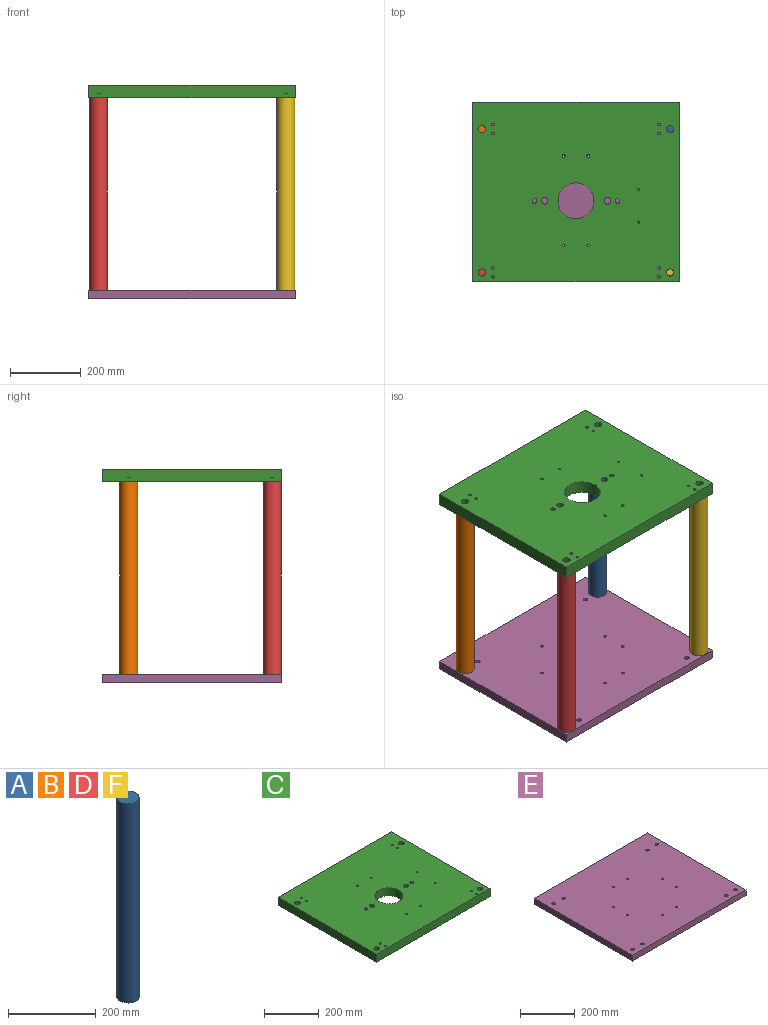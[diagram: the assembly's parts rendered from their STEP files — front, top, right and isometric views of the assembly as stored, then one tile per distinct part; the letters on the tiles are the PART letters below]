
ASSEMBLY  parts=6 mates=9
PART A: 3 faces, bbox 50.8x50.8x555.6 mm
  f0: cylinder r=25.4mm len=555.63mm, axis (0,0,-1), area 88673.8mm2, adj f1,f2
  f1: plane 50.8x50.8mm, normal (0,0,1), area 2026.8mm2, adj f0
  f2: plane 50.8x50.8mm, normal (0,0,-1), area 2026.8mm2, adj f0
PART B: same geometry as A
PART C: 29 faces, bbox 584.2x508x35.7 mm
  f0: plane 584.2x35.7mm, normal (0,-1,0), area 20855.8mm2, adj f1,f25,f27,f28
  f1: plane 508x35.7mm, normal (1,0,0), area 18135.4mm2, adj f0,f2,f27,f28
  f2: plane 584.2x35.7mm, normal (0,1,0), area 20855.8mm2, adj f1,f25,f27,f28
  f3: cylinder r=3.81mm len=35.7mm, axis (0,0,-1), area 854.6mm2, adj f27,f28
  f4: cylinder r=3.81mm len=35.7mm, axis (0,0,-1), area 854.6mm2, adj f27,f28
  f5: cylinder r=3.81mm len=35.7mm, axis (0,0,-1), area 854.6mm2, adj f27,f28
  f6: cylinder r=3.17mm len=35.7mm, axis (0,0,-1), area 712.2mm2, adj f27,f28
  f7: cylinder r=3.17mm len=35.7mm, axis (0,0,-1), area 712.2mm2, adj f27,f28
  f8: cylinder r=3.81mm len=35.7mm, axis (0,0,-1), area 854.6mm2, adj f27,f28
  f9: cylinder r=3.81mm len=35.7mm, axis (0,0,-1), area 854.6mm2, adj f27,f28
  f10: cylinder r=3.81mm len=35.7mm, axis (0,0,-1), area 854.6mm2, adj f27,f28
  f11: cylinder r=3.81mm len=35.7mm, axis (0,0,-1), area 854.6mm2, adj f27,f28
  f12: cylinder r=10.16mm len=35.7mm, axis (0,0,-1), area 2279mm2, adj f27,f28
  f13: cylinder r=10.16mm len=35.7mm, axis (0,0,-1), area 2279mm2, adj f27,f28
  f14: cylinder r=10.16mm len=35.7mm, axis (0,0,-1), area 2279mm2, adj f27,f28
  f15: cylinder r=10.16mm len=35.7mm, axis (0,0,-1), area 2279mm2, adj f27,f28
  f16: cylinder r=50.8mm len=101.6mm, axis (0,0,-1), area 11394.8mm2, adj f27,f28
  f17: cylinder r=9.5mm len=35.7mm, axis (0,0,-1), area 2130.8mm2, adj f27,f28
  f18: cylinder r=6.71mm len=35.7mm, axis (0,0,-1), area 1504.1mm2, adj f27,f28
  f19: cylinder r=9.5mm len=35.7mm, axis (0,0,-1), area 2130.8mm2, adj f27,f28
  f20: cylinder r=6.71mm len=35.7mm, axis (0,0,-1), area 1504.1mm2, adj f27,f28
  f21: cylinder r=3.81mm len=35.7mm, axis (0,0,-1), area 854.6mm2, adj f27,f28
  f22: cylinder r=3.81mm len=35.7mm, axis (0,0,-1), area 854.6mm2, adj f27,f28
  f23: cylinder r=3.81mm len=35.7mm, axis (0,0,-1), area 854.6mm2, adj f27,f28
  f24: cylinder r=3.81mm len=35.7mm, axis (0,0,-1), area 854.6mm2, adj f27,f28
  f25: plane 508x35.7mm, normal (-1,0,0), area 18135.4mm2, adj f0,f2,f27,f28
  f26: cylinder r=3.81mm len=35.7mm, axis (0,0,-1), area 854.6mm2, adj f27,f28
  f27: plane 584.2x508mm, normal (0,0,1), area 285909mm2, adj f0,f1,f2,f3,f4,f5,f6,f7
  f28: plane 584.2x508mm, normal (0,0,-1), area 285909mm2, adj f0,f1,f2,f3,f4,f5,f6,f7
PART D: same geometry as A
PART E: 38 faces, bbox 584.2x508x25.4 mm
  f0: cylinder r=6.35mm len=19.05mm, axis (0,0,-1), area 760.1mm2, adj f21,f23
  f1: cylinder r=6.35mm len=19.05mm, axis (0,0,-1), area 760.1mm2, adj f21,f37
  f2: cylinder r=6.35mm len=19.05mm, axis (0,0,-1), area 760.1mm2, adj f21,f35
  f3: cylinder r=6.35mm len=19.05mm, axis (0,0,-1), area 760.1mm2, adj f21,f33
  f4: cylinder r=6.35mm len=19.05mm, axis (0,0,-1), area 760.1mm2, adj f21,f24
  f5: cylinder r=6.35mm len=19.05mm, axis (0,0,-1), area 760.1mm2, adj f21,f28
  f6: cylinder r=6.35mm len=19.05mm, axis (0,0,-1), area 760.1mm2, adj f21,f26
  f7: cylinder r=6.35mm len=19.05mm, axis (0,0,-1), area 760.1mm2, adj f21,f30
  f8: plane 584.2x508mm, normal (0,0,-1), area 292355.1mm2, adj f9,f10,f11,f12,f13,f14,f15,f16
  f9: plane 584.2x25.4mm, normal (0,1,0), area 14838.7mm2, adj f8,f10,f20,f21
  f10: plane 508x25.4mm, normal (-1,0,0), area 12903.2mm2, adj f8,f9,f11,f21
  f11: plane 584.2x25.4mm, normal (0,-1,0), area 14838.7mm2, adj f8,f10,f20,f21
  f12: cylinder r=3.81mm len=25.4mm, axis (0,0,-1), area 608mm2, adj f8,f21
  f13: cylinder r=3.81mm len=25.4mm, axis (0,0,-1), area 608mm2, adj f8,f21
  f14: cylinder r=3.81mm len=25.4mm, axis (0,0,-1), area 608mm2, adj f8,f21
  f15: cylinder r=3.81mm len=25.4mm, axis (0,0,-1), area 608mm2, adj f8,f21
  f16: cylinder r=3.81mm len=25.4mm, axis (0,0,-1), area 608mm2, adj f8,f21
  f17: cylinder r=3.81mm len=25.4mm, axis (0,0,-1), area 608mm2, adj f8,f21
  f18: cylinder r=3.81mm len=25.4mm, axis (0,0,-1), area 608mm2, adj f8,f21
  f19: cylinder r=3.81mm len=25.4mm, axis (0,0,-1), area 608mm2, adj f8,f21
  f20: plane 508x25.4mm, normal (1,0,0), area 12903.2mm2, adj f8,f9,f11,f21
  f21: plane 584.2x508mm, normal (0,0,1), area 295395.4mm2, adj f0,f1,f2,f3,f4,f5,f6,f7
  f22: cylinder r=12.7mm len=25.4mm, axis (0,0,-1), area 506.7mm2, adj f8,f23
  f23: plane 25.4x25.4mm, normal (0,0,-1), area 380mm2, adj f0,f22
  f24: plane 25.4x25.4mm, normal (0,0,-1), area 380mm2, adj f4,f25
  f25: cylinder r=12.7mm len=25.4mm, axis (0,0,-1), area 506.7mm2, adj f8,f24
  f26: plane 25.4x25.4mm, normal (0,0,-1), area 380mm2, adj f6,f27
  f27: cylinder r=12.7mm len=25.4mm, axis (0,0,-1), area 506.7mm2, adj f8,f26
  f28: plane 25.4x25.4mm, normal (0,0,-1), area 380mm2, adj f5,f29
  f29: cylinder r=12.7mm len=25.4mm, axis (0,0,-1), area 506.7mm2, adj f8,f28
  f30: plane 25.4x25.4mm, normal (0,0,-1), area 380mm2, adj f7,f31
  f31: cylinder r=12.7mm len=25.4mm, axis (0,0,-1), area 506.7mm2, adj f8,f30
  f32: cylinder r=12.7mm len=25.4mm, axis (0,0,-1), area 506.7mm2, adj f8,f33
  f33: plane 25.4x25.4mm, normal (0,0,-1), area 380mm2, adj f3,f32
  f34: cylinder r=12.7mm len=25.4mm, axis (0,0,-1), area 506.7mm2, adj f8,f35
  f35: plane 25.4x25.4mm, normal (0,0,-1), area 380mm2, adj f2,f34
  f36: cylinder r=12.7mm len=25.4mm, axis (0,0,-1), area 506.7mm2, adj f8,f37
  f37: plane 25.4x25.4mm, normal (0,0,-1), area 380mm2, adj f1,f36
PART F: same geometry as A
PLACE A t=(278.9,245.2,-192.34)mm
PLACE B t=(-251.96,245.2,-192.34)mm
PLACE C t=(13.47,66.13,352.98)mm
PLACE D t=(-251.96,-161.2,-192.34)mm
PLACE E t=(13.47,83.25,-217.74)mm
PLACE F t=(278.9,-161.2,-192.34)mm
MATE planar E.f1 <-> D.f0  axis (0,0,1) through (-251.96,-161.2,-192.34)mm
MATE cylindrical C.f8 <-> E.f12  axis (0,0,1) through (-21.46,-86.27,388.68)mm
MATE cylindrical E.f7 <-> F.f0  axis (0,0,1) through (278.9,-161.2,-192.34)mm
MATE cylindrical B.f0 <-> E.f2  axis (0,0,-1) through (-251.96,245.2,-192.34)mm
MATE cylindrical D.f0 <-> E.f1  axis (0,0,-1) through (-251.96,-161.2,-192.34)mm
MATE planar E.f2 <-> B.f0  axis (0,0,1) through (-251.96,245.2,-192.34)mm
MATE cylindrical A.f0 <-> E.f6  axis (0,0,-1) through (278.9,245.2,-192.34)mm
MATE planar E.f7 <-> F.f0  axis (0,0,1) through (278.9,-161.2,-192.34)mm
MATE planar E.f6 <-> A.f0  axis (0,0,-1) through (278.9,245.2,-192.34)mm
